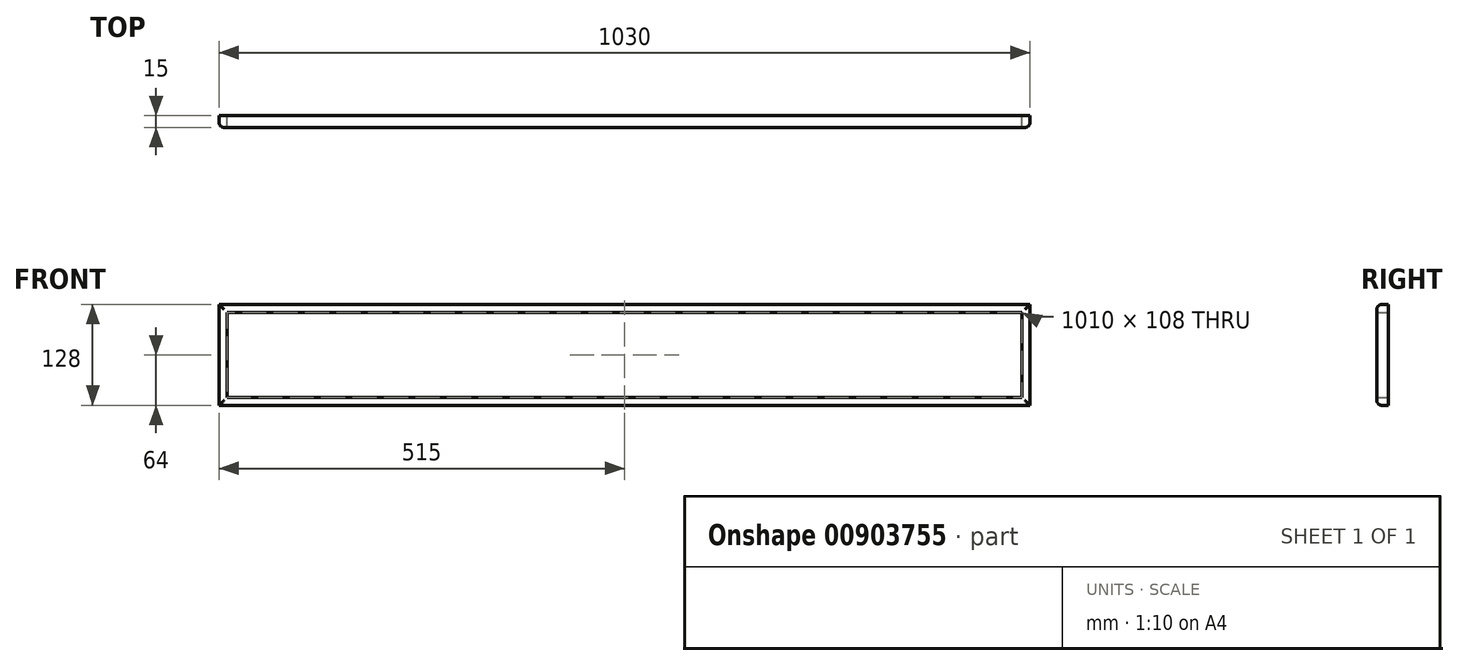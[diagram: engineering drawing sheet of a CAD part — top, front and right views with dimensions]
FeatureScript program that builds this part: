
annotation { "Feature Type Name" : "Feature", "Feature Type Description" : "" }
export const myFeature = defineFeature(function(context is Context, id is Id, definition is map)
    precondition{}
    {
        {
            var Q0;
            Q0=qCreatedBy(makeId("Front.planeOp"),FACE);
            var sketch = newSketch(context, id + "F0", { "sketchPlane" : qUnion([Q0])});
            skLineSegment(sketch, "E0.bottom", {"start": v(-505, 48) * mm, "end": v(505, 48) * mm});
            skLineSegment(sketch, "E0.top", {"start": v(-505, -60) * mm, "end": v(505, -60) * mm});
            skLineSegment(sketch, "E0.left", {"start": v(-505, 48) * mm, "end": v(-505, -60) * mm});
            skLineSegment(sketch, "E0.right", {"start": v(505, 48) * mm, "end": v(505, -60) * mm});
            skLineSegment(sketch, "E1.0", {"start": v(-515, 58) * mm, "end": v(-515, -70) * mm});
            skLineSegment(sketch, "E1.1", {"start": v(-515, 58) * mm, "end": v(515, 58) * mm});
            skLineSegment(sketch, "E1.2", {"start": v(515, 58) * mm, "end": v(515, -70) * mm});
            skLineSegment(sketch, "E1.3", {"start": v(-515, -70) * mm, "end": v(515, -70) * mm});
            skSolve(sketch);
        }
        {
            var Q0;
            Q0=makeQuery(id+"F0.imprint","IMPRINT",FACE,{"disambiguationData":[TD([[makeQuery(id+"F0.imprint","IMPRINT",EDGE,{"derivedFrom":sQuery(id+"F0.wireOp",EDGE,"E0.bottom")}),-1.0]])]});
            extrude(context, id + "F1", {"entities" : qUnion([Q0]), "depth" : 15 * mm, "offsetDistance" : 25 * mm});
        }
        {
            var Q0;
            Q0=makeQuery(id+"F0.imprint","IMPRINT",FACE,{"disambiguationData":[TD([[makeQuery(id+"F0.imprint","IMPRINT",EDGE,{"derivedFrom":sQuery(id+"F0.wireOp",EDGE,"E0.bottom")}),1.0]])]});
            extrude(context, id + "F2", {"entities" : qUnion([Q0]), "depth" : 15 * mm, "offsetDistance" : 25 * mm});
        }
        {
            var Q0;
            Q0=makeQuery(id+"F2.opExtrude","CAP_EDGE",EDGE,{"disambiguationData":[OSD([sQuery(id+"F0.wireOp",EDGE,"E1.1")])],"isStart":false});
            var Q1;
            Q1=makeQuery(id+"F2.opExtrude","CAP_EDGE",EDGE,{"disambiguationData":[OSD([sQuery(id+"F0.wireOp",EDGE,"E1.0")])],"isStart":false});
            var Q2;
            Q2=makeQuery(id+"F2.opExtrude","CAP_EDGE",EDGE,{"disambiguationData":[OSD([sQuery(id+"F0.wireOp",EDGE,"E1.3")])],"isStart":false});
            var Q3;
            Q3=makeQuery(id+"F2.opExtrude","CAP_EDGE",EDGE,{"disambiguationData":[OSD([sQuery(id+"F0.wireOp",EDGE,"E1.2")])],"isStart":false});
            fillet(context, id + "F3", {"entities" : qUnion([Q0, Q1, Q2, Q3]), "radius" : 6.3 * mm, "tangentPropagation" : true, "allowEdgeOverflow" : false});
        }
    });
